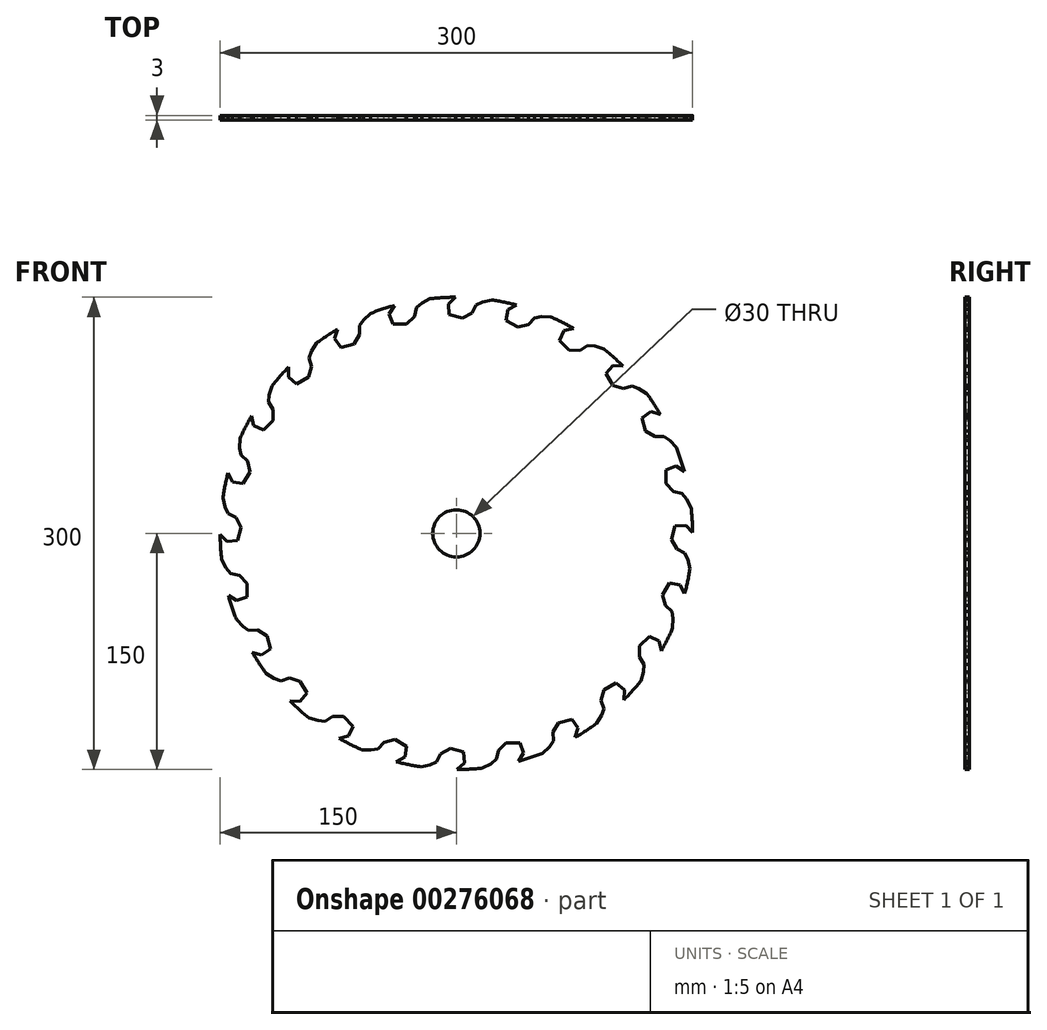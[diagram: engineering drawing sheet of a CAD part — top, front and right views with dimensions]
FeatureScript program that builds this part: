
annotation { "Feature Type Name" : "Feature", "Feature Type Description" : "" }
export const myFeature = defineFeature(function(context is Context, id is Id, definition is map)
    precondition{}
    {
        {
            var Q0;
            Q0=qCreatedBy(makeId("Front.planeOp"),FACE);
            var sketch = newSketch(context, id + "F0", { "sketchPlane" : qUnion([Q0])});
            skCircle(sketch, "E0", {"center": v(0, 0) * mm, "radius": 15 * mm});
            skCircle(sketch, "E1", {"center": v(0, 0) * mm, "radius": 150 * mm});
            skSolve(sketch);
        }
        {
            var Q0;
            Q0=makeQuery(id+"F0.imprint","IMPRINT",FACE,{"disambiguationData":[TD([[makeQuery(id+"F0.imprint","IMPRINT",EDGE,{"derivedFrom":sQuery(id+"F0.wireOp",EDGE,"E0")}),-1.0]])]});
            extrude(context, id + "F1", {"entities" : qUnion([Q0]), "depth" : 3 * mm});
        }
        {
            var Q0;
            Q0=qCreatedBy(makeId("Front.planeOp"),FACE);
            var sketch = newSketch(context, id + "F2", { "sketchPlane" : qUnion([Q0])});
            skLineSegment(sketch, "E2", {"start": v(0, 150.5) * mm, "end": v(-5.15, 145.75) * mm});
            skLineSegment(sketch, "E3", {"start": v(-5.15, 145.75) * mm, "end": v(-4.55, 138.9) * mm});
            skLineSegment(sketch, "E4", {"start": v(-4.55, 138.9) * mm, "end": v(3.83, 136.64) * mm});
            skLineSegment(sketch, "E5", {"start": v(3.83, 136.64) * mm, "end": v(9.95, 140.02) * mm});
            skLineSegment(sketch, "E6", {"start": v(9.95, 140.02) * mm, "end": v(12.58, 145.02) * mm});
            skLineSegment(sketch, "E7", {"start": v(12.58, 145.02) * mm, "end": v(16.72, 146.95) * mm});
            skLineSegment(sketch, "E8", {"start": v(16.72, 146.95) * mm, "end": v(23.85, 148.6) * mm});
            skLineSegment(sketch, "E9", {"start": v(23.85, 148.6) * mm, "end": v(10.16, 150.16) * mm});
            skLineSegment(sketch, "E10", {"start": v(10.16, 150.16) * mm, "end": v(0, 150.5) * mm});
            skLineSegment(sketch, "E11.1.0", {"start": v(-15.42, 149.7) * mm, "end": v(-29.05, 147.67) * mm});
            skLineSegment(sketch, "E11.1.1", {"start": v(-21.88, 146.28) * mm, "end": v(-15.42, 149.7) * mm});
            skLineSegment(sketch, "E11.1.2", {"start": v(-42.7, 139.46) * mm, "end": v(-40.34, 132.99) * mm});
            skLineSegment(sketch, "E11.1.3", {"start": v(-40.34, 132.99) * mm, "end": v(-31.67, 132.98) * mm});
            skLineSegment(sketch, "E11.1.4", {"start": v(-29.05, 147.67) * mm, "end": v(-38.95, 145.37) * mm});
            skLineSegment(sketch, "E11.1.5", {"start": v(-26.63, 137.83) * mm, "end": v(-25.39, 143.34) * mm});
            skLineSegment(sketch, "E11.1.6", {"start": v(-31.67, 132.98) * mm, "end": v(-26.63, 137.83) * mm});
            skLineSegment(sketch, "E11.1.7", {"start": v(-38.95, 145.37) * mm, "end": v(-42.7, 139.46) * mm});
            skLineSegment(sketch, "E11.1.8", {"start": v(-25.39, 143.34) * mm, "end": v(-21.88, 146.28) * mm});
            skLineSegment(sketch, "E11.2.0", {"start": v(-53.64, 140.62) * mm, "end": v(-66.28, 135.12) * mm});
            skLineSegment(sketch, "E11.2.1", {"start": v(-59, 135.63) * mm, "end": v(-53.64, 140.62) * mm});
            skLineSegment(sketch, "E11.2.2", {"start": v(-77.33, 123.65) * mm, "end": v(-73.39, 118.01) * mm});
            skLineSegment(sketch, "E11.2.3", {"start": v(-73.39, 118.01) * mm, "end": v(-65, 120.25) * mm});
            skLineSegment(sketch, "E11.2.4", {"start": v(-66.28, 135.12) * mm, "end": v(-75.25, 130.34) * mm});
            skLineSegment(sketch, "E11.2.5", {"start": v(-61.4, 126.24) * mm, "end": v(-61.62, 131.88) * mm});
            skLineSegment(sketch, "E11.2.6", {"start": v(-65, 120.25) * mm, "end": v(-61.4, 126.24) * mm});
            skLineSegment(sketch, "E11.2.7", {"start": v(-75.25, 130.34) * mm, "end": v(-77.33, 123.65) * mm});
            skLineSegment(sketch, "E11.2.8", {"start": v(-61.62, 131.88) * mm, "end": v(-59, 135.63) * mm});
            skLineSegment(sketch, "E11.3.0", {"start": v(-88.2, 121.94) * mm, "end": v(-99, 113.36) * mm});
            skLineSegment(sketch, "E11.3.1", {"start": v(-92.09, 115.74) * mm, "end": v(-88.2, 121.94) * mm});
            skLineSegment(sketch, "E11.3.2", {"start": v(-106.7, 99.42) * mm, "end": v(-101.43, 95) * mm});
            skLineSegment(sketch, "E11.3.3", {"start": v(-101.43, 95) * mm, "end": v(-93.91, 99.33) * mm});
            skLineSegment(sketch, "E11.3.4", {"start": v(-99, 113.36) * mm, "end": v(-106.42, 106.42) * mm});
            skLineSegment(sketch, "E11.3.5", {"start": v(-91.97, 106.05) * mm, "end": v(-93.65, 111.44) * mm});
            skLineSegment(sketch, "E11.3.6", {"start": v(-93.91, 99.33) * mm, "end": v(-91.97, 106.05) * mm});
            skLineSegment(sketch, "E11.3.7", {"start": v(-106.42, 106.42) * mm, "end": v(-106.7, 99.42) * mm});
            skLineSegment(sketch, "E11.3.8", {"start": v(-93.65, 111.44) * mm, "end": v(-92.09, 115.74) * mm});
            skLineSegment(sketch, "E11.4.0", {"start": v(-116.76, 94.96) * mm, "end": v(-124.96, 83.88) * mm});
            skLineSegment(sketch, "E11.4.1", {"start": v(-118.9, 87.96) * mm, "end": v(-116.76, 94.96) * mm});
            skLineSegment(sketch, "E11.4.2", {"start": v(-128.8, 68.42) * mm, "end": v(-122.56, 65.5) * mm});
            skLineSegment(sketch, "E11.4.3", {"start": v(-122.56, 65.5) * mm, "end": v(-116.42, 71.64) * mm});
            skLineSegment(sketch, "E11.4.4", {"start": v(-124.96, 83.88) * mm, "end": v(-130.34, 75.25) * mm});
            skLineSegment(sketch, "E11.4.5", {"start": v(-116.29, 78.63) * mm, "end": v(-119.3, 83.4) * mm});
            skLineSegment(sketch, "E11.4.6", {"start": v(-116.42, 71.64) * mm, "end": v(-116.29, 78.63) * mm});
            skLineSegment(sketch, "E11.4.7", {"start": v(-130.34, 75.25) * mm, "end": v(-128.8, 68.42) * mm});
            skLineSegment(sketch, "E11.4.8", {"start": v(-119.3, 83.4) * mm, "end": v(-118.9, 87.96) * mm});
            skLineSegment(sketch, "E11.5.0", {"start": v(-137.36, 61.5) * mm, "end": v(-142.4, 48.68) * mm});
            skLineSegment(sketch, "E11.5.1", {"start": v(-137.62, 54.19) * mm, "end": v(-137.36, 61.5) * mm});
            skLineSegment(sketch, "E11.5.2", {"start": v(-142.12, 32.75) * mm, "end": v(-135.34, 31.55) * mm});
            skLineSegment(sketch, "E11.5.3", {"start": v(-135.34, 31.55) * mm, "end": v(-131, 39.06) * mm});
            skLineSegment(sketch, "E11.5.4", {"start": v(-142.4, 48.68) * mm, "end": v(-145.37, 38.95) * mm});
            skLineSegment(sketch, "E11.5.5", {"start": v(-132.68, 45.86) * mm, "end": v(-136.83, 49.68) * mm});
            skLineSegment(sketch, "E11.5.6", {"start": v(-131, 39.06) * mm, "end": v(-132.68, 45.86) * mm});
            skLineSegment(sketch, "E11.5.7", {"start": v(-145.37, 38.95) * mm, "end": v(-142.12, 32.75) * mm});
            skLineSegment(sketch, "E11.5.8", {"start": v(-136.83, 49.68) * mm, "end": v(-137.62, 54.19) * mm});
            skLineSegment(sketch, "E11.6.0", {"start": v(-148.6, 23.85) * mm, "end": v(-150.16, 10.16) * mm});
            skLineSegment(sketch, "E11.6.1", {"start": v(-146.95, 16.72) * mm, "end": v(-148.6, 23.85) * mm});
            skLineSegment(sketch, "E11.6.2", {"start": v(-145.75, -5.15) * mm, "end": v(-138.9, -4.55) * mm});
            skLineSegment(sketch, "E11.6.3", {"start": v(-138.9, -4.55) * mm, "end": v(-136.64, 3.83) * mm});
            skLineSegment(sketch, "E11.6.4", {"start": v(-150.16, 10.16) * mm, "end": v(-150.5, 0) * mm});
            skLineSegment(sketch, "E11.6.5", {"start": v(-140.02, 9.95) * mm, "end": v(-145.02, 12.58) * mm});
            skLineSegment(sketch, "E11.6.6", {"start": v(-136.64, 3.83) * mm, "end": v(-140.02, 9.95) * mm});
            skLineSegment(sketch, "E11.6.7", {"start": v(-150.5, 0) * mm, "end": v(-145.75, -5.15) * mm});
            skLineSegment(sketch, "E11.6.8", {"start": v(-145.02, 12.58) * mm, "end": v(-146.95, 16.72) * mm});
            skLineSegment(sketch, "E11.7.0", {"start": v(-149.7, -15.42) * mm, "end": v(-147.67, -29.05) * mm});
            skLineSegment(sketch, "E11.7.1", {"start": v(-146.28, -21.88) * mm, "end": v(-149.7, -15.42) * mm});
            skLineSegment(sketch, "E11.7.2", {"start": v(-139.46, -42.7) * mm, "end": v(-132.99, -40.34) * mm});
            skLineSegment(sketch, "E11.7.3", {"start": v(-132.99, -40.34) * mm, "end": v(-132.98, -31.67) * mm});
            skLineSegment(sketch, "E11.7.4", {"start": v(-147.67, -29.05) * mm, "end": v(-145.37, -38.95) * mm});
            skLineSegment(sketch, "E11.7.5", {"start": v(-137.83, -26.63) * mm, "end": v(-143.34, -25.39) * mm});
            skLineSegment(sketch, "E11.7.6", {"start": v(-132.98, -31.67) * mm, "end": v(-137.83, -26.63) * mm});
            skLineSegment(sketch, "E11.7.7", {"start": v(-145.37, -38.95) * mm, "end": v(-139.46, -42.7) * mm});
            skLineSegment(sketch, "E11.7.8", {"start": v(-143.34, -25.39) * mm, "end": v(-146.28, -21.88) * mm});
            skLineSegment(sketch, "E11.8.0", {"start": v(-140.62, -53.64) * mm, "end": v(-135.12, -66.28) * mm});
            skLineSegment(sketch, "E11.8.1", {"start": v(-135.63, -59) * mm, "end": v(-140.62, -53.64) * mm});
            skLineSegment(sketch, "E11.8.2", {"start": v(-123.65, -77.33) * mm, "end": v(-118.01, -73.39) * mm});
            skLineSegment(sketch, "E11.8.3", {"start": v(-118.01, -73.39) * mm, "end": v(-120.25, -65) * mm});
            skLineSegment(sketch, "E11.8.4", {"start": v(-135.12, -66.28) * mm, "end": v(-130.34, -75.25) * mm});
            skLineSegment(sketch, "E11.8.5", {"start": v(-126.24, -61.4) * mm, "end": v(-131.88, -61.62) * mm});
            skLineSegment(sketch, "E11.8.6", {"start": v(-120.25, -65) * mm, "end": v(-126.24, -61.4) * mm});
            skLineSegment(sketch, "E11.8.7", {"start": v(-130.34, -75.25) * mm, "end": v(-123.65, -77.33) * mm});
            skLineSegment(sketch, "E11.8.8", {"start": v(-131.88, -61.62) * mm, "end": v(-135.63, -59) * mm});
            skLineSegment(sketch, "E11.9.0", {"start": v(-121.94, -88.2) * mm, "end": v(-113.36, -99) * mm});
            skLineSegment(sketch, "E11.9.1", {"start": v(-115.74, -92.09) * mm, "end": v(-121.94, -88.2) * mm});
            skLineSegment(sketch, "E11.9.2", {"start": v(-99.42, -106.7) * mm, "end": v(-95, -101.43) * mm});
            skLineSegment(sketch, "E11.9.3", {"start": v(-95, -101.43) * mm, "end": v(-99.33, -93.91) * mm});
            skLineSegment(sketch, "E11.9.4", {"start": v(-113.36, -99) * mm, "end": v(-106.42, -106.42) * mm});
            skLineSegment(sketch, "E11.9.5", {"start": v(-106.05, -91.97) * mm, "end": v(-111.44, -93.65) * mm});
            skLineSegment(sketch, "E11.9.6", {"start": v(-99.33, -93.91) * mm, "end": v(-106.05, -91.97) * mm});
            skLineSegment(sketch, "E11.9.7", {"start": v(-106.42, -106.42) * mm, "end": v(-99.42, -106.7) * mm});
            skLineSegment(sketch, "E11.9.8", {"start": v(-111.44, -93.65) * mm, "end": v(-115.74, -92.09) * mm});
            skLineSegment(sketch, "E11.10.0", {"start": v(-94.96, -116.76) * mm, "end": v(-83.88, -124.96) * mm});
            skLineSegment(sketch, "E11.10.1", {"start": v(-87.96, -118.9) * mm, "end": v(-94.96, -116.76) * mm});
            skLineSegment(sketch, "E11.10.2", {"start": v(-68.42, -128.8) * mm, "end": v(-65.5, -122.56) * mm});
            skLineSegment(sketch, "E11.10.3", {"start": v(-65.5, -122.56) * mm, "end": v(-71.64, -116.42) * mm});
            skLineSegment(sketch, "E11.10.4", {"start": v(-83.88, -124.96) * mm, "end": v(-75.25, -130.34) * mm});
            skLineSegment(sketch, "E11.10.5", {"start": v(-78.63, -116.29) * mm, "end": v(-83.4, -119.3) * mm});
            skLineSegment(sketch, "E11.10.6", {"start": v(-71.64, -116.42) * mm, "end": v(-78.63, -116.29) * mm});
            skLineSegment(sketch, "E11.10.7", {"start": v(-75.25, -130.34) * mm, "end": v(-68.42, -128.8) * mm});
            skLineSegment(sketch, "E11.10.8", {"start": v(-83.4, -119.3) * mm, "end": v(-87.96, -118.9) * mm});
            skLineSegment(sketch, "E11.11.0", {"start": v(-61.5, -137.36) * mm, "end": v(-48.68, -142.4) * mm});
            skLineSegment(sketch, "E11.11.1", {"start": v(-54.19, -137.62) * mm, "end": v(-61.5, -137.36) * mm});
            skLineSegment(sketch, "E11.11.2", {"start": v(-32.75, -142.12) * mm, "end": v(-31.55, -135.34) * mm});
            skLineSegment(sketch, "E11.11.3", {"start": v(-31.55, -135.34) * mm, "end": v(-39.06, -131) * mm});
            skLineSegment(sketch, "E11.11.4", {"start": v(-48.68, -142.4) * mm, "end": v(-38.95, -145.37) * mm});
            skLineSegment(sketch, "E11.11.5", {"start": v(-45.86, -132.68) * mm, "end": v(-49.68, -136.83) * mm});
            skLineSegment(sketch, "E11.11.6", {"start": v(-39.06, -131) * mm, "end": v(-45.86, -132.68) * mm});
            skLineSegment(sketch, "E11.11.7", {"start": v(-38.95, -145.37) * mm, "end": v(-32.75, -142.12) * mm});
            skLineSegment(sketch, "E11.11.8", {"start": v(-49.68, -136.83) * mm, "end": v(-54.19, -137.62) * mm});
            skLineSegment(sketch, "E11.12.0", {"start": v(-23.85, -148.6) * mm, "end": v(-10.16, -150.16) * mm});
            skLineSegment(sketch, "E11.12.1", {"start": v(-16.72, -146.95) * mm, "end": v(-23.85, -148.6) * mm});
            skLineSegment(sketch, "E11.12.2", {"start": v(5.15, -145.75) * mm, "end": v(4.55, -138.9) * mm});
            skLineSegment(sketch, "E11.12.3", {"start": v(4.55, -138.9) * mm, "end": v(-3.83, -136.64) * mm});
            skLineSegment(sketch, "E11.12.4", {"start": v(-10.16, -150.16) * mm, "end": v(0, -150.5) * mm});
            skLineSegment(sketch, "E11.12.5", {"start": v(-9.95, -140.02) * mm, "end": v(-12.58, -145.02) * mm});
            skLineSegment(sketch, "E11.12.6", {"start": v(-3.83, -136.64) * mm, "end": v(-9.95, -140.02) * mm});
            skLineSegment(sketch, "E11.12.7", {"start": v(0, -150.5) * mm, "end": v(5.15, -145.75) * mm});
            skLineSegment(sketch, "E11.12.8", {"start": v(-12.58, -145.02) * mm, "end": v(-16.72, -146.95) * mm});
            skLineSegment(sketch, "E11.13.0", {"start": v(15.42, -149.7) * mm, "end": v(29.05, -147.67) * mm});
            skLineSegment(sketch, "E11.13.1", {"start": v(21.88, -146.28) * mm, "end": v(15.42, -149.7) * mm});
            skLineSegment(sketch, "E11.13.2", {"start": v(42.7, -139.46) * mm, "end": v(40.34, -132.99) * mm});
            skLineSegment(sketch, "E11.13.3", {"start": v(40.34, -132.99) * mm, "end": v(31.67, -132.98) * mm});
            skLineSegment(sketch, "E11.13.4", {"start": v(29.05, -147.67) * mm, "end": v(38.95, -145.37) * mm});
            skLineSegment(sketch, "E11.13.5", {"start": v(26.63, -137.83) * mm, "end": v(25.39, -143.34) * mm});
            skLineSegment(sketch, "E11.13.6", {"start": v(31.67, -132.98) * mm, "end": v(26.63, -137.83) * mm});
            skLineSegment(sketch, "E11.13.7", {"start": v(38.95, -145.37) * mm, "end": v(42.7, -139.46) * mm});
            skLineSegment(sketch, "E11.13.8", {"start": v(25.39, -143.34) * mm, "end": v(21.88, -146.28) * mm});
            skLineSegment(sketch, "E11.14.0", {"start": v(53.64, -140.62) * mm, "end": v(66.28, -135.12) * mm});
            skLineSegment(sketch, "E11.14.1", {"start": v(59, -135.63) * mm, "end": v(53.64, -140.62) * mm});
            skLineSegment(sketch, "E11.14.2", {"start": v(77.33, -123.65) * mm, "end": v(73.39, -118.01) * mm});
            skLineSegment(sketch, "E11.14.3", {"start": v(73.39, -118.01) * mm, "end": v(65, -120.25) * mm});
            skLineSegment(sketch, "E11.14.4", {"start": v(66.28, -135.12) * mm, "end": v(75.25, -130.34) * mm});
            skLineSegment(sketch, "E11.14.5", {"start": v(61.4, -126.24) * mm, "end": v(61.62, -131.88) * mm});
            skLineSegment(sketch, "E11.14.6", {"start": v(65, -120.25) * mm, "end": v(61.4, -126.24) * mm});
            skLineSegment(sketch, "E11.14.7", {"start": v(75.25, -130.34) * mm, "end": v(77.33, -123.65) * mm});
            skLineSegment(sketch, "E11.14.8", {"start": v(61.62, -131.88) * mm, "end": v(59, -135.63) * mm});
            skLineSegment(sketch, "E11.15.0", {"start": v(88.2, -121.94) * mm, "end": v(99, -113.36) * mm});
            skLineSegment(sketch, "E11.15.1", {"start": v(92.09, -115.74) * mm, "end": v(88.2, -121.94) * mm});
            skLineSegment(sketch, "E11.15.2", {"start": v(106.7, -99.42) * mm, "end": v(101.43, -95) * mm});
            skLineSegment(sketch, "E11.15.3", {"start": v(101.43, -95) * mm, "end": v(93.91, -99.33) * mm});
            skLineSegment(sketch, "E11.15.4", {"start": v(99, -113.36) * mm, "end": v(106.42, -106.42) * mm});
            skLineSegment(sketch, "E11.15.5", {"start": v(91.97, -106.05) * mm, "end": v(93.65, -111.44) * mm});
            skLineSegment(sketch, "E11.15.6", {"start": v(93.91, -99.33) * mm, "end": v(91.97, -106.05) * mm});
            skLineSegment(sketch, "E11.15.7", {"start": v(106.42, -106.42) * mm, "end": v(106.7, -99.42) * mm});
            skLineSegment(sketch, "E11.15.8", {"start": v(93.65, -111.44) * mm, "end": v(92.09, -115.74) * mm});
            skLineSegment(sketch, "E11.16.0", {"start": v(116.76, -94.96) * mm, "end": v(124.96, -83.88) * mm});
            skLineSegment(sketch, "E11.16.1", {"start": v(118.9, -87.96) * mm, "end": v(116.76, -94.96) * mm});
            skLineSegment(sketch, "E11.16.2", {"start": v(128.8, -68.42) * mm, "end": v(122.56, -65.5) * mm});
            skLineSegment(sketch, "E11.16.3", {"start": v(122.56, -65.5) * mm, "end": v(116.42, -71.64) * mm});
            skLineSegment(sketch, "E11.16.4", {"start": v(124.96, -83.88) * mm, "end": v(130.34, -75.25) * mm});
            skLineSegment(sketch, "E11.16.5", {"start": v(116.29, -78.63) * mm, "end": v(119.3, -83.4) * mm});
            skLineSegment(sketch, "E11.16.6", {"start": v(116.42, -71.64) * mm, "end": v(116.29, -78.63) * mm});
            skLineSegment(sketch, "E11.16.7", {"start": v(130.34, -75.25) * mm, "end": v(128.8, -68.42) * mm});
            skLineSegment(sketch, "E11.16.8", {"start": v(119.3, -83.4) * mm, "end": v(118.9, -87.96) * mm});
            skLineSegment(sketch, "E11.17.0", {"start": v(137.36, -61.5) * mm, "end": v(142.4, -48.68) * mm});
            skLineSegment(sketch, "E11.17.1", {"start": v(137.62, -54.19) * mm, "end": v(137.36, -61.5) * mm});
            skLineSegment(sketch, "E11.17.2", {"start": v(142.12, -32.75) * mm, "end": v(135.34, -31.55) * mm});
            skLineSegment(sketch, "E11.17.3", {"start": v(135.34, -31.55) * mm, "end": v(131, -39.06) * mm});
            skLineSegment(sketch, "E11.17.4", {"start": v(142.4, -48.68) * mm, "end": v(145.37, -38.95) * mm});
            skLineSegment(sketch, "E11.17.5", {"start": v(132.68, -45.86) * mm, "end": v(136.83, -49.68) * mm});
            skLineSegment(sketch, "E11.17.6", {"start": v(131, -39.06) * mm, "end": v(132.68, -45.86) * mm});
            skLineSegment(sketch, "E11.17.7", {"start": v(145.37, -38.95) * mm, "end": v(142.12, -32.75) * mm});
            skLineSegment(sketch, "E11.17.8", {"start": v(136.83, -49.68) * mm, "end": v(137.62, -54.19) * mm});
            skLineSegment(sketch, "E11.18.0", {"start": v(148.6, -23.85) * mm, "end": v(150.16, -10.16) * mm});
            skLineSegment(sketch, "E11.18.1", {"start": v(146.95, -16.72) * mm, "end": v(148.6, -23.85) * mm});
            skLineSegment(sketch, "E11.18.2", {"start": v(145.75, 5.15) * mm, "end": v(138.9, 4.55) * mm});
            skLineSegment(sketch, "E11.18.3", {"start": v(138.9, 4.55) * mm, "end": v(136.64, -3.83) * mm});
            skLineSegment(sketch, "E11.18.4", {"start": v(150.16, -10.16) * mm, "end": v(150.5, 0) * mm});
            skLineSegment(sketch, "E11.18.5", {"start": v(140.02, -9.95) * mm, "end": v(145.02, -12.58) * mm});
            skLineSegment(sketch, "E11.18.6", {"start": v(136.64, -3.83) * mm, "end": v(140.02, -9.95) * mm});
            skLineSegment(sketch, "E11.18.7", {"start": v(150.5, 0) * mm, "end": v(145.75, 5.15) * mm});
            skLineSegment(sketch, "E11.18.8", {"start": v(145.02, -12.58) * mm, "end": v(146.95, -16.72) * mm});
            skLineSegment(sketch, "E11.19.0", {"start": v(149.7, 15.42) * mm, "end": v(147.67, 29.05) * mm});
            skLineSegment(sketch, "E11.19.1", {"start": v(146.28, 21.88) * mm, "end": v(149.7, 15.42) * mm});
            skLineSegment(sketch, "E11.19.2", {"start": v(139.46, 42.7) * mm, "end": v(132.99, 40.34) * mm});
            skLineSegment(sketch, "E11.19.3", {"start": v(132.99, 40.34) * mm, "end": v(132.98, 31.67) * mm});
            skLineSegment(sketch, "E11.19.4", {"start": v(147.67, 29.05) * mm, "end": v(145.37, 38.95) * mm});
            skLineSegment(sketch, "E11.19.5", {"start": v(137.83, 26.63) * mm, "end": v(143.34, 25.39) * mm});
            skLineSegment(sketch, "E11.19.6", {"start": v(132.98, 31.67) * mm, "end": v(137.83, 26.63) * mm});
            skLineSegment(sketch, "E11.19.7", {"start": v(145.37, 38.95) * mm, "end": v(139.46, 42.7) * mm});
            skLineSegment(sketch, "E11.19.8", {"start": v(143.34, 25.39) * mm, "end": v(146.28, 21.88) * mm});
            skLineSegment(sketch, "E11.20.0", {"start": v(140.62, 53.64) * mm, "end": v(135.12, 66.28) * mm});
            skLineSegment(sketch, "E11.20.1", {"start": v(135.63, 59) * mm, "end": v(140.62, 53.64) * mm});
            skLineSegment(sketch, "E11.20.2", {"start": v(123.65, 77.33) * mm, "end": v(118.01, 73.39) * mm});
            skLineSegment(sketch, "E11.20.3", {"start": v(118.01, 73.39) * mm, "end": v(120.25, 65) * mm});
            skLineSegment(sketch, "E11.20.4", {"start": v(135.12, 66.28) * mm, "end": v(130.34, 75.25) * mm});
            skLineSegment(sketch, "E11.20.5", {"start": v(126.24, 61.4) * mm, "end": v(131.88, 61.62) * mm});
            skLineSegment(sketch, "E11.20.6", {"start": v(120.25, 65) * mm, "end": v(126.24, 61.4) * mm});
            skLineSegment(sketch, "E11.20.7", {"start": v(130.34, 75.25) * mm, "end": v(123.65, 77.33) * mm});
            skLineSegment(sketch, "E11.20.8", {"start": v(131.88, 61.62) * mm, "end": v(135.63, 59) * mm});
            skLineSegment(sketch, "E11.21.0", {"start": v(121.94, 88.2) * mm, "end": v(113.36, 99) * mm});
            skLineSegment(sketch, "E11.21.1", {"start": v(115.74, 92.09) * mm, "end": v(121.94, 88.2) * mm});
            skLineSegment(sketch, "E11.21.2", {"start": v(99.42, 106.7) * mm, "end": v(95, 101.43) * mm});
            skLineSegment(sketch, "E11.21.3", {"start": v(95, 101.43) * mm, "end": v(99.33, 93.91) * mm});
            skLineSegment(sketch, "E11.21.4", {"start": v(113.36, 99) * mm, "end": v(106.42, 106.42) * mm});
            skLineSegment(sketch, "E11.21.5", {"start": v(106.05, 91.97) * mm, "end": v(111.44, 93.65) * mm});
            skLineSegment(sketch, "E11.21.6", {"start": v(99.33, 93.91) * mm, "end": v(106.05, 91.97) * mm});
            skLineSegment(sketch, "E11.21.7", {"start": v(106.42, 106.42) * mm, "end": v(99.42, 106.7) * mm});
            skLineSegment(sketch, "E11.21.8", {"start": v(111.44, 93.65) * mm, "end": v(115.74, 92.09) * mm});
            skLineSegment(sketch, "E11.22.0", {"start": v(94.96, 116.76) * mm, "end": v(83.88, 124.96) * mm});
            skLineSegment(sketch, "E11.22.1", {"start": v(87.96, 118.9) * mm, "end": v(94.96, 116.76) * mm});
            skLineSegment(sketch, "E11.22.2", {"start": v(68.42, 128.8) * mm, "end": v(65.5, 122.56) * mm});
            skLineSegment(sketch, "E11.22.3", {"start": v(65.5, 122.56) * mm, "end": v(71.64, 116.42) * mm});
            skLineSegment(sketch, "E11.22.4", {"start": v(83.88, 124.96) * mm, "end": v(75.25, 130.34) * mm});
            skLineSegment(sketch, "E11.22.5", {"start": v(78.63, 116.29) * mm, "end": v(83.4, 119.3) * mm});
            skLineSegment(sketch, "E11.22.6", {"start": v(71.64, 116.42) * mm, "end": v(78.63, 116.29) * mm});
            skLineSegment(sketch, "E11.22.7", {"start": v(75.25, 130.34) * mm, "end": v(68.42, 128.8) * mm});
            skLineSegment(sketch, "E11.22.8", {"start": v(83.4, 119.3) * mm, "end": v(87.96, 118.9) * mm});
            skLineSegment(sketch, "E11.23.0", {"start": v(61.5, 137.36) * mm, "end": v(48.68, 142.4) * mm});
            skLineSegment(sketch, "E11.23.1", {"start": v(54.19, 137.62) * mm, "end": v(61.5, 137.36) * mm});
            skLineSegment(sketch, "E11.23.2", {"start": v(32.75, 142.12) * mm, "end": v(31.55, 135.34) * mm});
            skLineSegment(sketch, "E11.23.3", {"start": v(31.55, 135.34) * mm, "end": v(39.06, 131) * mm});
            skLineSegment(sketch, "E11.23.4", {"start": v(48.68, 142.4) * mm, "end": v(38.95, 145.37) * mm});
            skLineSegment(sketch, "E11.23.5", {"start": v(45.86, 132.68) * mm, "end": v(49.68, 136.83) * mm});
            skLineSegment(sketch, "E11.23.6", {"start": v(39.06, 131) * mm, "end": v(45.86, 132.68) * mm});
            skLineSegment(sketch, "E11.23.7", {"start": v(38.95, 145.37) * mm, "end": v(32.75, 142.12) * mm});
            skLineSegment(sketch, "E11.23.8", {"start": v(49.68, 136.83) * mm, "end": v(54.19, 137.62) * mm});
            skPoint(sketch, "E11.center", {"position": v(0, 0) * mm});
            skSolve(sketch);
        }
        {
            var Q0;
            Q0 = qSketchRegion(id + "F2", true);
            extrude(context, id + "F3", {"entities" : qUnion([Q0]), "operationType" : NewBodyOperationType.REMOVE, "endBound" : BoundingType.UP_TO_NEXT, "depth" : 25 * mm});
        }
    });
